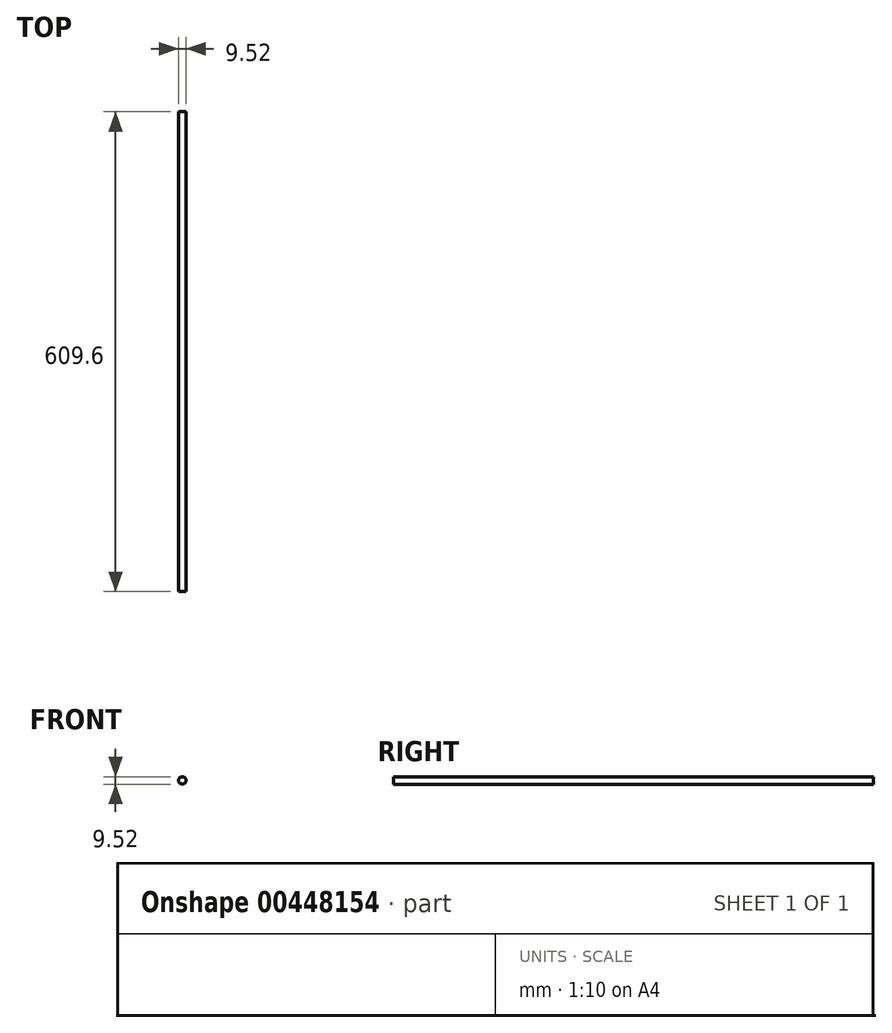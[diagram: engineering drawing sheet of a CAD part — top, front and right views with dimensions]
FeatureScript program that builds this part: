
annotation { "Feature Type Name" : "Feature", "Feature Type Description" : "" }
export const myFeature = defineFeature(function(context is Context, id is Id, definition is map)
    precondition{}
    {
        {
            var Q0;
            Q0=qCreatedBy(makeId("Front.planeOp"),FACE);
            var sketch = newSketch(context, id + "F0", { "sketchPlane" : qUnion([Q0])});
            skCircle(sketch, "E0", {"center": v(0, 0) * mm, "radius": 4.76 * mm});
            skSolve(sketch);
        }
        {
            var Q0;
            Q0=makeQuery(id+"F0.imprint","IMPRINT",FACE,{"disambiguationData":[TD([[makeQuery(id+"F0.imprint","IMPRINT",EDGE,{"derivedFrom":sQuery(id+"F0.wireOp",EDGE,"E0")}),1.0]])]});
            extrude(context, id + "F1", {"entities" : qUnion([Q0]), "depth" : 609.6 * mm});
        }
    });
